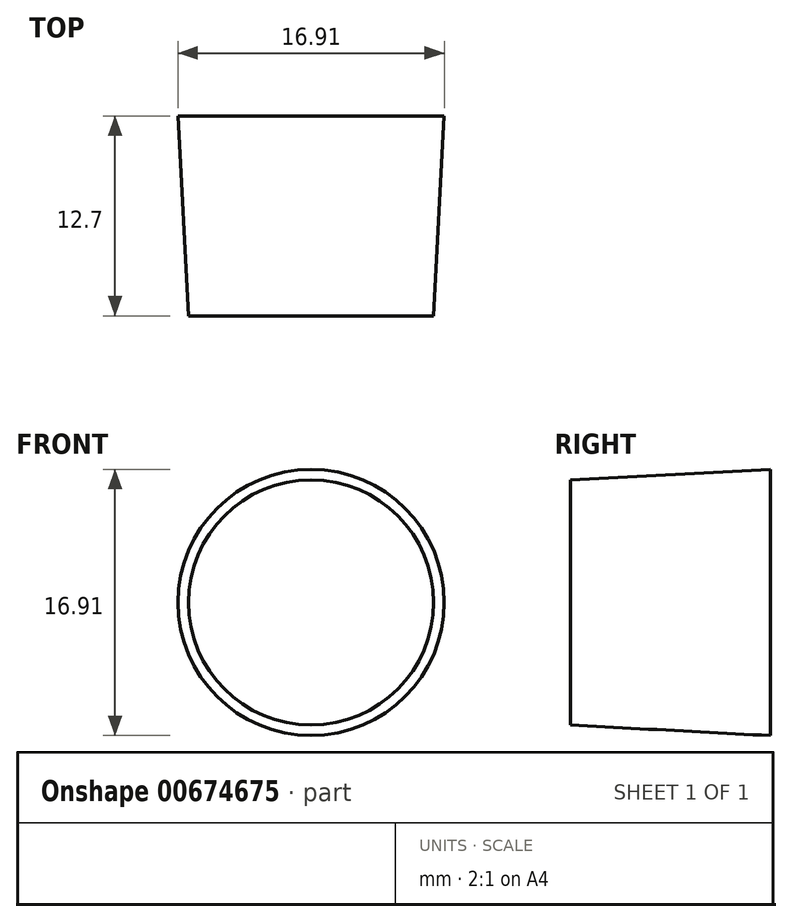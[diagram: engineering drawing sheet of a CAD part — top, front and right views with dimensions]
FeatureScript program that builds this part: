
annotation { "Feature Type Name" : "Feature", "Feature Type Description" : "" }
export const myFeature = defineFeature(function(context is Context, id is Id, definition is map)
    precondition{}
    {
        {
            var Q0;
            Q0=qCreatedBy(makeId("Front.planeOp"),FACE);
            var sketch = newSketch(context, id + "F0", { "sketchPlane" : qUnion([Q0])});
            skCircle(sketch, "E0", {"center": v(-39.9, 21.52) * mm, "radius": 7.79 * mm});
            skPoint(sketch, "E0.first.point", {"position": v(-39.44, 13.74) * mm});
            skPoint(sketch, "E0.second.point", {"position": v(-39.62, 29.3) * mm});
            skPoint(sketch, "E0.third.point", {"position": v(-47.59, 22.82) * mm});
            skSolve(sketch);
        }
        {
            var Q0;
            Q0=makeQuery(id+"F0.imprint","IMPRINT",FACE,{"disambiguationData":[TD([[makeQuery(id+"F0.imprint","IMPRINT",EDGE,{"derivedFrom":sQuery(id+"F0.wireOp",EDGE,"E0")}),1.0]])]});
            extrude(context, id + "F1", {"entities" : qUnion([Q0]), "oppositeDirection" : true, "depth" : 12.7 * mm, "offsetDistance" : 25.4 * mm, "hasDraft" : true, "draftAngle" : 3 * degree});
        }
    });
